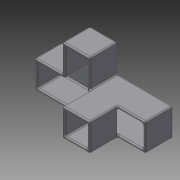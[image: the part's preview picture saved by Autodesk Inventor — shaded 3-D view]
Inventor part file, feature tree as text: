
AUTODESK INVENTOR PART (.ipt)
format: ipt  version: 2014 (Build 180170000, 170)  size: 257,536 bytes
history: native  units: in
note: dims shown in document units (in); Inventor stores cm internally (conversion verified against a paired STEP export)
features: plane x8, extrude x2, other x1, shell x1, fillet x1, sketch x1
ambient origin geometry x8: Origin, YZ Plane, XZ Plane, XY Plane, X Axis, Y Axis, Z Axis, Center Point
bodies: Solid1 (feature_tree)
feature tree (14):
  other  "Cube Master.ipt"
  extrude  "Extrusion1"  Depth=0.3937in
  extrude  "Extrusion2"  Depth=0.0193in TaperAngle=0.0deg
  shell  "Shell1"  Thickness=0.0in
  fillet  "Fillet1"  Radius=0.0394in
  sketch  "Sketch1"  dims[d0=0.3937in d1=0.3937in d2=1.0in d3=0.0in d4=0.0in d5=0.0in d6=0.0394in d7=0.0193in d8=0.0193in]
  plane  "Work Plane1"
  plane  "Work Plane2"
  plane  "Work Plane3"
  plane  "Work Plane4"
  plane  "Work Plane5"
  plane  "Work Plane6"
  plane  "Work Plane7"
  plane  "Work Plane8"
